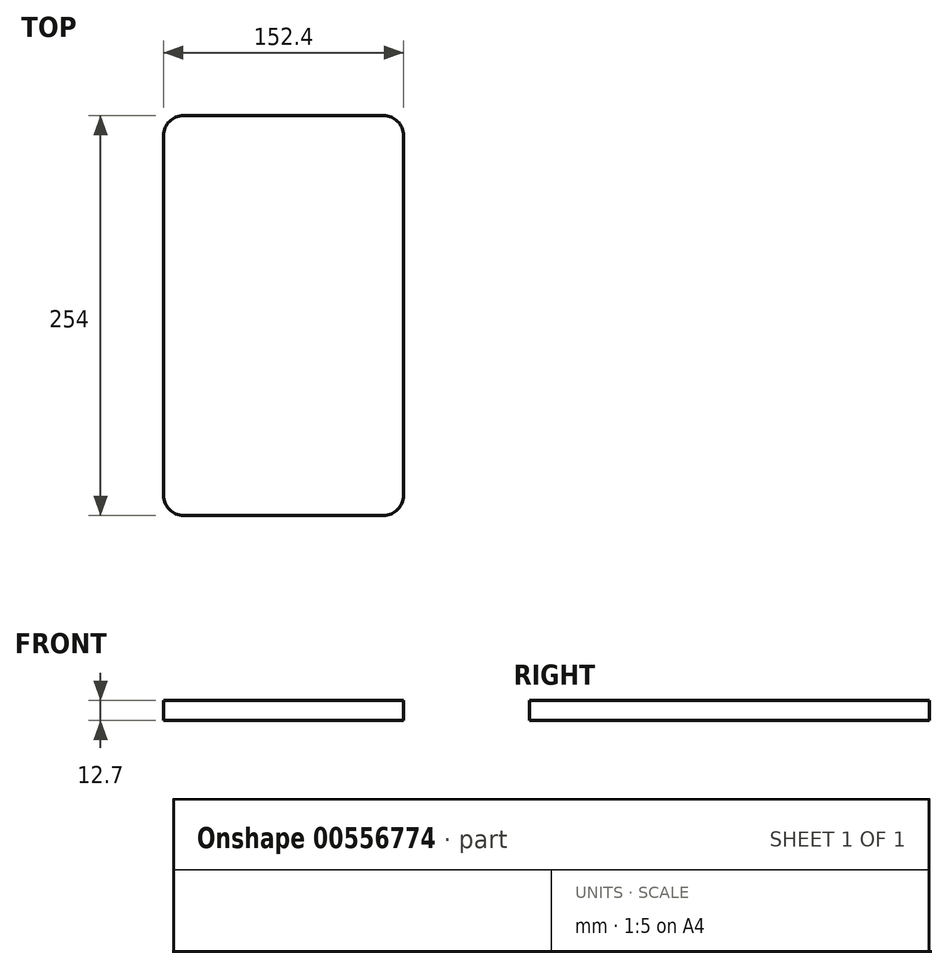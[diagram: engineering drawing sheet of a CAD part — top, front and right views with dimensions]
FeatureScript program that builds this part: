
annotation { "Feature Type Name" : "Feature", "Feature Type Description" : "" }
export const myFeature = defineFeature(function(context is Context, id is Id, definition is map)
    precondition{}
    {
        {
            var Q0;
            Q0=qCreatedBy(makeId("Top.planeOp"),FACE);
            var sketch = newSketch(context, id + "F0", { "sketchPlane" : qUnion([Q0])});
            skLineSegment(sketch, "E0.bottom", {"start": v(-76.2, 127) * mm, "end": v(76.2, 127) * mm});
            skLineSegment(sketch, "E0.top", {"start": v(-76.2, -127) * mm, "end": v(76.2, -127) * mm});
            skLineSegment(sketch, "E0.left", {"start": v(-76.2, 127) * mm, "end": v(-76.2, -127) * mm});
            skLineSegment(sketch, "E0.right", {"start": v(76.2, 127) * mm, "end": v(76.2, -127) * mm});
            skSolve(sketch);
        }
        {
            var Q0;
            Q0 = qSketchRegion(id + "F0", true);
            extrude(context, id + "F1", {"entities" : qUnion([Q0]), "depth" : 12.7 * mm, "offsetDistance" : 25.4 * mm});
        }
        {
            var Q0;
            Q0=makeQuery(id+"F1.opExtrude","SWEPT_EDGE",EDGE,{"disambiguationData":[OSD([sQuery(id+"F0.wireOp",EDGE,"E0.top"),sQuery(id+"F0.wireOp",EDGE,"E0.right")])]});
            var Q1;
            Q1=makeQuery(id+"F1.opExtrude","SWEPT_EDGE",EDGE,{"disambiguationData":[OSD([sQuery(id+"F0.wireOp",EDGE,"E0.top"),sQuery(id+"F0.wireOp",EDGE,"E0.left")])]});
            var Q2;
            Q2=makeQuery(id+"F1.opExtrude","SWEPT_EDGE",EDGE,{"disambiguationData":[OSD([sQuery(id+"F0.wireOp",EDGE,"E0.bottom"),sQuery(id+"F0.wireOp",EDGE,"E0.right")])]});
            var Q3;
            Q3=makeQuery(id+"F1.opExtrude","SWEPT_EDGE",EDGE,{"disambiguationData":[OSD([sQuery(id+"F0.wireOp",EDGE,"E0.bottom"),sQuery(id+"F0.wireOp",EDGE,"E0.left")])]});
            fillet(context, id + "F2", {"entities" : qUnion([Q0, Q1, Q2, Q3]), "radius" : 12.7 * mm, "tangentPropagation" : true, "allowEdgeOverflow" : false});
        }
    });
